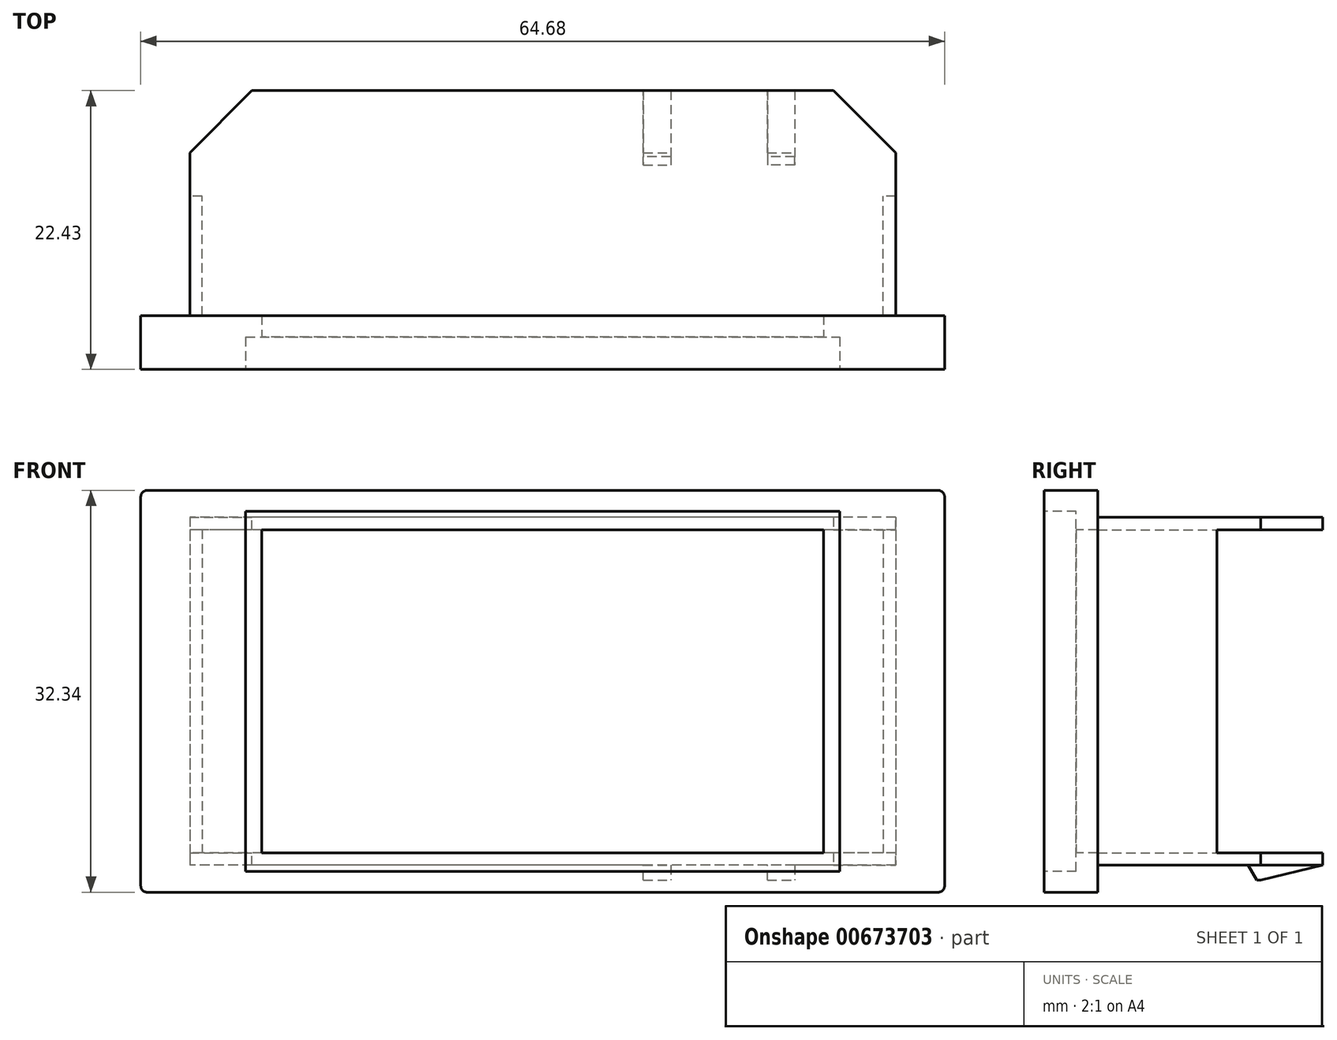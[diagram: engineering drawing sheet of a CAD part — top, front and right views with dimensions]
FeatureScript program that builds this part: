
annotation { "Feature Type Name" : "Feature", "Feature Type Description" : "" }
export const myFeature = defineFeature(function(context is Context, id is Id, definition is map)
    precondition{}
    {
        {
            var Q0;
            Q0=qCreatedBy(makeId("Front.planeOp"),FACE);
            var sketch = newSketch(context, id + "F0", { "sketchPlane" : qUnion([Q0])});
            skLineSegment(sketch, "E0.bottom", {"start": v(-32.34, 16.17) * mm, "end": v(32.34, 16.17) * mm});
            skLineSegment(sketch, "E0.top", {"start": v(-32.34, -16.17) * mm, "end": v(32.34, -16.17) * mm});
            skLineSegment(sketch, "E0.left", {"start": v(-32.34, 16.17) * mm, "end": v(-32.34, -16.17) * mm});
            skLineSegment(sketch, "E0.right", {"start": v(32.34, 16.17) * mm, "end": v(32.34, -16.17) * mm});
            skSolve(sketch);
        }
        {
            var Q0;
            Q0=qSketchRegion(id+"F0",true);
            extrude(context, id + "F1", {"entities" : qUnion([Q0]), "depth" : 4.33 * mm});
        }
        {
            var Q0;
            Q0=makeQuery(id+"F1.opExtrude","SWEPT_EDGE",EDGE,{"disambiguationData":[OSD([sQuery(id+"F0.wireOp",EDGE,"E0.bottom"),sQuery(id+"F0.wireOp",EDGE,"E0.left")])]});
            var Q1;
            Q1=makeQuery(id+"F1.opExtrude","SWEPT_EDGE",EDGE,{"disambiguationData":[OSD([sQuery(id+"F0.wireOp",EDGE,"E0.top"),sQuery(id+"F0.wireOp",EDGE,"E0.left")])]});
            var Q2;
            Q2=makeQuery(id+"F1.opExtrude","SWEPT_EDGE",EDGE,{"disambiguationData":[OSD([sQuery(id+"F0.wireOp",EDGE,"E0.bottom"),sQuery(id+"F0.wireOp",EDGE,"E0.right")])]});
            var Q3;
            Q3=makeQuery(id+"F1.opExtrude","SWEPT_EDGE",EDGE,{"disambiguationData":[OSD([sQuery(id+"F0.wireOp",EDGE,"E0.top"),sQuery(id+"F0.wireOp",EDGE,"E0.right")])]});
            fillet(context, id + "F2", {"entities" : qUnion([Q0, Q1, Q2, Q3]), "radius" : .5 * mm, "tangentPropagation" : true, "allowEdgeOverflow" : false});
        }
        {
            var Q0;
            Q0=makeQuery(id+"F1.opExtrude","CAP_FACE",FACE,{"disambiguationData":[OSD([sQuery(id+"F0.wireOp",EDGE,"E0.bottom"),sQuery(id+"F0.wireOp",EDGE,"E0.top"),sQuery(id+"F0.wireOp",EDGE,"E0.left"),sQuery(id+"F0.wireOp",EDGE,"E0.right")])],"isStart":true});
            var sketch = newSketch(context, id + "F3", { "sketchPlane" : qUnion([Q0])});
            skLineSegment(sketch, "E1.bottom", {"start": v(-28.4, 14) * mm, "end": v(28.4, 14) * mm});
            skLineSegment(sketch, "E1.top", {"start": v(-28.4, -14) * mm, "end": v(28.4, -14) * mm});
            skLineSegment(sketch, "E1.left", {"start": v(-28.4, 14) * mm, "end": v(-28.4, -14) * mm});
            skLineSegment(sketch, "E1.right", {"start": v(28.4, 14) * mm, "end": v(28.4, -14) * mm});
            skSolve(sketch);
        }
        {
            var Q0;
            Q0=qSketchRegion(id+"F3",true);
            extrude(context, id + "F4", {"entities" : qUnion([Q0]), "operationType" : NewBodyOperationType.ADD, "depth" : 9.6 * mm});
        }
        {
            var Q0;
            Q0=makeQuery(id+"F4.opExtrude","CAP_FACE",FACE,{"disambiguationData":[OSD([sQuery(id+"F3.wireOp",EDGE,"E1.bottom"),sQuery(id+"F3.wireOp",EDGE,"E1.top"),sQuery(id+"F3.wireOp",EDGE,"E1.left"),sQuery(id+"F3.wireOp",EDGE,"E1.right")])],"isStart":false});
            var sketch = newSketch(context, id + "F5", { "sketchPlane" : qUnion([Q0])});
            skLineSegment(sketch, "E2.0", {"start": v(-27.4, 13) * mm, "end": v(27.4, 13) * mm});
            skLineSegment(sketch, "E2.1", {"start": v(-27.4, 13) * mm, "end": v(-27.4, -13) * mm});
            skLineSegment(sketch, "E2.2", {"start": v(-27.4, -13) * mm, "end": v(27.4, -13) * mm});
            skLineSegment(sketch, "E2.3", {"start": v(27.4, 13) * mm, "end": v(27.4, -13) * mm});
            skSolve(sketch);
        }
        {
            var Q0;
            Q0=makeQuery(id+"F5.imprint","IMPRINT",FACE,{"disambiguationData":[TD([[makeQuery(id+"F5.imprint","IMPRINT",EDGE,{"derivedFrom":sQuery(id+"F5.wireOp",EDGE,"E2.0")}),-1.0]])]});
            var Q1;
            Q1=makeQuery(id+"F1.opExtrude","CAP_FACE",FACE,{"disambiguationData":[OSD([sQuery(id+"F0.wireOp",EDGE,"E0.bottom"),sQuery(id+"F0.wireOp",EDGE,"E0.top"),sQuery(id+"F0.wireOp",EDGE,"E0.left"),sQuery(id+"F0.wireOp",EDGE,"E0.right")])],"isStart":true});
            extrude(context, id + "F6", {"entities" : qUnion([Q0]), "operationType" : NewBodyOperationType.REMOVE, "endBound" : BoundingType.UP_TO_SURFACE, "oppositeDirection" : true, "endBoundEntityFace" : qUnion([Q1]), "depth" : 25 * mm});
        }
        {
            var Q0;
            Q0=makeQuery(id+"F4.opExtrude","CAP_FACE",FACE,{"disambiguationData":[OSD([sQuery(id+"F3.wireOp",EDGE,"E1.bottom"),sQuery(id+"F3.wireOp",EDGE,"E1.top"),sQuery(id+"F3.wireOp",EDGE,"E1.left"),sQuery(id+"F3.wireOp",EDGE,"E1.right")])],"isStart":false});
            var sketch = newSketch(context, id + "F7", { "sketchPlane" : qUnion([Q0])});
            skLineSegment(sketch, "E3.bottom", {"start": v(-28.4, 14) * mm, "end": v(28.4, 14) * mm});
            skLineSegment(sketch, "E3.top", {"start": v(-28.4, 13) * mm, "end": v(28.4, 13) * mm});
            skLineSegment(sketch, "E3.left", {"start": v(-28.4, 14) * mm, "end": v(-28.4, 13) * mm});
            skLineSegment(sketch, "E3.right", {"start": v(28.4, 14) * mm, "end": v(28.4, 13) * mm});
            skLineSegment(sketch, "E4.bottom", {"start": v(-28.4, -14) * mm, "end": v(28.4, -14) * mm});
            skLineSegment(sketch, "E4.top", {"start": v(-28.4, -13) * mm, "end": v(28.4, -13) * mm});
            skLineSegment(sketch, "E4.left", {"start": v(-28.4, -14) * mm, "end": v(-28.4, -13) * mm});
            skLineSegment(sketch, "E4.right", {"start": v(28.4, -14) * mm, "end": v(28.4, -13) * mm});
            skSolve(sketch);
        }
        {
            var Q0;
            Q0=qSketchRegion(id+"F7",true);
            extrude(context, id + "F8", {"entities" : qUnion([Q0]), "operationType" : NewBodyOperationType.ADD, "depth" : 8.5 * mm});
        }
        {
            var Q0;
            Q0=makeQuery(id+"F8.opExtrude","CAP_EDGE",EDGE,{"disambiguationData":[OSD([sQuery(id+"F7.wireOp",EDGE,"E4.left")])],"isStart":false});
            var Q1;
            Q1=makeQuery(id+"F8.opExtrude","CAP_EDGE",EDGE,{"disambiguationData":[OSD([sQuery(id+"F7.wireOp",EDGE,"E3.left")])],"isStart":false});
            var Q2;
            Q2=makeQuery(id+"F8.opExtrude","CAP_EDGE",EDGE,{"disambiguationData":[OSD([sQuery(id+"F7.wireOp",EDGE,"E4.right")])],"isStart":false});
            var Q3;
            Q3=makeQuery(id+"F8.opExtrude","CAP_EDGE",EDGE,{"disambiguationData":[OSD([sQuery(id+"F7.wireOp",EDGE,"E3.right")])],"isStart":false});
            chamfer(context, id + "F9", {"entities" : qUnion([Q0, Q1, Q2, Q3]), "width" : 5 * mm, "tangentPropagation" : true});
        }
        {
            var Q0;
            Q0=makeQuery(id+"F8.boolean.opBoolean","MERGE",FACE,{"derivedFrom":[makeQuery(id+"F4.opExtrude","SWEPT_FACE",FACE,{"disambiguationData":[OSD([sQuery(id+"F3.wireOp",EDGE,"E1.top")])]}),makeQuery(id+"F8.opExtrude","SWEPT_FACE",FACE,{"disambiguationData":[OSD([sQuery(id+"F7.wireOp",EDGE,"E4.bottom")])]})]});
            var sketch = newSketch(context, id + "F10", { "sketchPlane" : qUnion([Q0])});
            skLineSegment(sketch, "E5.bottom", {"start": v(20.29, -18.1) * mm, "end": v(18.09, -18.1) * mm});
            skLineSegment(sketch, "E5.top", {"start": v(20.29, -12.1) * mm, "end": v(18.09, -12.1) * mm});
            skLineSegment(sketch, "E5.left", {"start": v(20.29, -18.1) * mm, "end": v(20.29, -12.1) * mm});
            skLineSegment(sketch, "E5.right", {"start": v(18.09, -18.1) * mm, "end": v(18.09, -12.1) * mm});
            skLineSegment(sketch, "E6.bottom", {"start": v(8.1, -18.1) * mm, "end": v(10.3, -18.1) * mm});
            skLineSegment(sketch, "E6.top", {"start": v(8.1, -12.1) * mm, "end": v(10.3, -12.1) * mm});
            skLineSegment(sketch, "E6.left", {"start": v(8.1, -18.1) * mm, "end": v(8.1, -12.1) * mm});
            skLineSegment(sketch, "E6.right", {"start": v(10.3, -18.1) * mm, "end": v(10.3, -12.1) * mm});
            skLineSegment(sketch, "E7", {"start": v(14.2, 1.65) * mm, "end": v(14.2, -22.8) * mm, "construction": true});
            skSolve(sketch);
        }
        {
            var Q0;
            Q0=qSketchRegion(id+"F10",true);
            extrude(context, id + "F11", {"entities" : qUnion([Q0]), "operationType" : NewBodyOperationType.ADD, "depth" : 1.2 * mm});
        }
        {
            var Q0;
            Q0=makeQuery(id+"F11.opExtrude","CAP_EDGE",EDGE,{"disambiguationData":[OSD([sQuery(id+"F10.wireOp",EDGE,"E5.top")])],"isStart":false});
            chamfer(context, id + "F12", {"entities" : qUnion([Q0]), "chamferType" : ChamferType.OFFSET_ANGLE, "width" : 1.2 * mm, "oppositeDirection" : true, "angle" : 30 * degree, "tangentPropagation" : true});
        }
        {
            var Q0;
            Q0=makeQuery(id+"F11.opExtrude","CAP_EDGE",EDGE,{"disambiguationData":[OSD([sQuery(id+"F10.wireOp",EDGE,"E6.top")])],"isStart":false});
            chamfer(context, id + "F13", {"entities" : qUnion([Q0]), "chamferType" : ChamferType.OFFSET_ANGLE, "width" : 1.2 * mm, "oppositeDirection" : false, "angle" : 30 * degree, "tangentPropagation" : true});
        }
        {
            var Q0;
            Q0=makeQuery(id+"F11.opExtrude","CAP_EDGE",EDGE,{"disambiguationData":[OSD([sQuery(id+"F10.wireOp",EDGE,"E6.bottom")])],"isStart":false});
            var Q1;
            Q1=makeQuery(id+"F11.opExtrude","CAP_EDGE",EDGE,{"disambiguationData":[OSD([sQuery(id+"F10.wireOp",EDGE,"E5.bottom")])],"isStart":false});
            chamfer(context, id + "F14", {"entities" : qUnion([Q0, Q1]), "chamferType" : ChamferType.TWO_OFFSETS, "width1" : 1.2 * mm, "oppositeDirection" : false, "width2" : 5 * mm, "tangentPropagation" : true});
        }
        {
            var Q0;
            Q0=makeQuery(id+"F1.opExtrude","CAP_FACE",FACE,{"disambiguationData":[OSD([sQuery(id+"F0.wireOp",EDGE,"E0.bottom"),sQuery(id+"F0.wireOp",EDGE,"E0.top"),sQuery(id+"F0.wireOp",EDGE,"E0.left"),sQuery(id+"F0.wireOp",EDGE,"E0.right")])],"isStart":false});
            var sketch = newSketch(context, id + "F15", { "sketchPlane" : qUnion([Q0])});
            skLineSegment(sketch, "E8.bottom", {"start": v(-23.9, -14.5) * mm, "end": v(23.9, -14.5) * mm});
            skLineSegment(sketch, "E8.top", {"start": v(-23.9, 14.5) * mm, "end": v(23.9, 14.5) * mm});
            skLineSegment(sketch, "E8.left", {"start": v(-23.9, -14.5) * mm, "end": v(-23.9, 14.5) * mm});
            skLineSegment(sketch, "E8.right", {"start": v(23.9, -14.5) * mm, "end": v(23.9, 14.5) * mm});
            skPoint(sketch, "E8.middle", {"position": v(0, 0) * mm});
            skSolve(sketch);
        }
        {
            var Q0;
            Q0=makeQuery(id+"F15.imprint","IMPRINT",FACE,{"disambiguationData":[TD([[makeQuery(id+"F15.imprint","IMPRINT",EDGE,{"derivedFrom":sQuery(id+"F15.wireOp",EDGE,"E8.bottom")}),1.0]])]});
            extrude(context, id + "F16", {"entities" : qUnion([Q0]), "operationType" : NewBodyOperationType.REMOVE, "oppositeDirection" : true, "depth" : 2.6 * mm});
        }
        {
            var Q0;
            Q0=makeQuery(id+"F16.boolean.opBoolean","COPY",FACE,{"derivedFrom":makeQuery(id+"F16.opExtrude","CAP_FACE",FACE,{"disambiguationData":[OSD([sQuery(id+"F15.wireOp",EDGE,"E8.bottom"),sQuery(id+"F15.wireOp",EDGE,"E8.top"),sQuery(id+"F15.wireOp",EDGE,"E8.left"),sQuery(id+"F15.wireOp",EDGE,"E8.right")])],"isStart":false})});
            var sketch = newSketch(context, id + "F17", { "sketchPlane" : qUnion([Q0])});
            skLineSegment(sketch, "E9.bottom", {"start": v(22.6, 13) * mm, "end": v(-22.6, 13) * mm});
            skLineSegment(sketch, "E9.top", {"start": v(22.6, -13) * mm, "end": v(-22.6, -13) * mm});
            skLineSegment(sketch, "E9.left", {"start": v(22.6, 13) * mm, "end": v(22.6, -13) * mm});
            skLineSegment(sketch, "E9.right", {"start": v(-22.6, 13) * mm, "end": v(-22.6, -13) * mm});
            skPoint(sketch, "E9.middle", {"position": v(0, 0) * mm});
            skSolve(sketch);
        }
        {
            var Q0;
            Q0=qSketchRegion(id+"F17",true);
            extrude(context, id + "F18", {"entities" : qUnion([Q0]), "operationType" : NewBodyOperationType.REMOVE, "oppositeDirection" : true, "depth" : 25 * mm});
        }
    });
